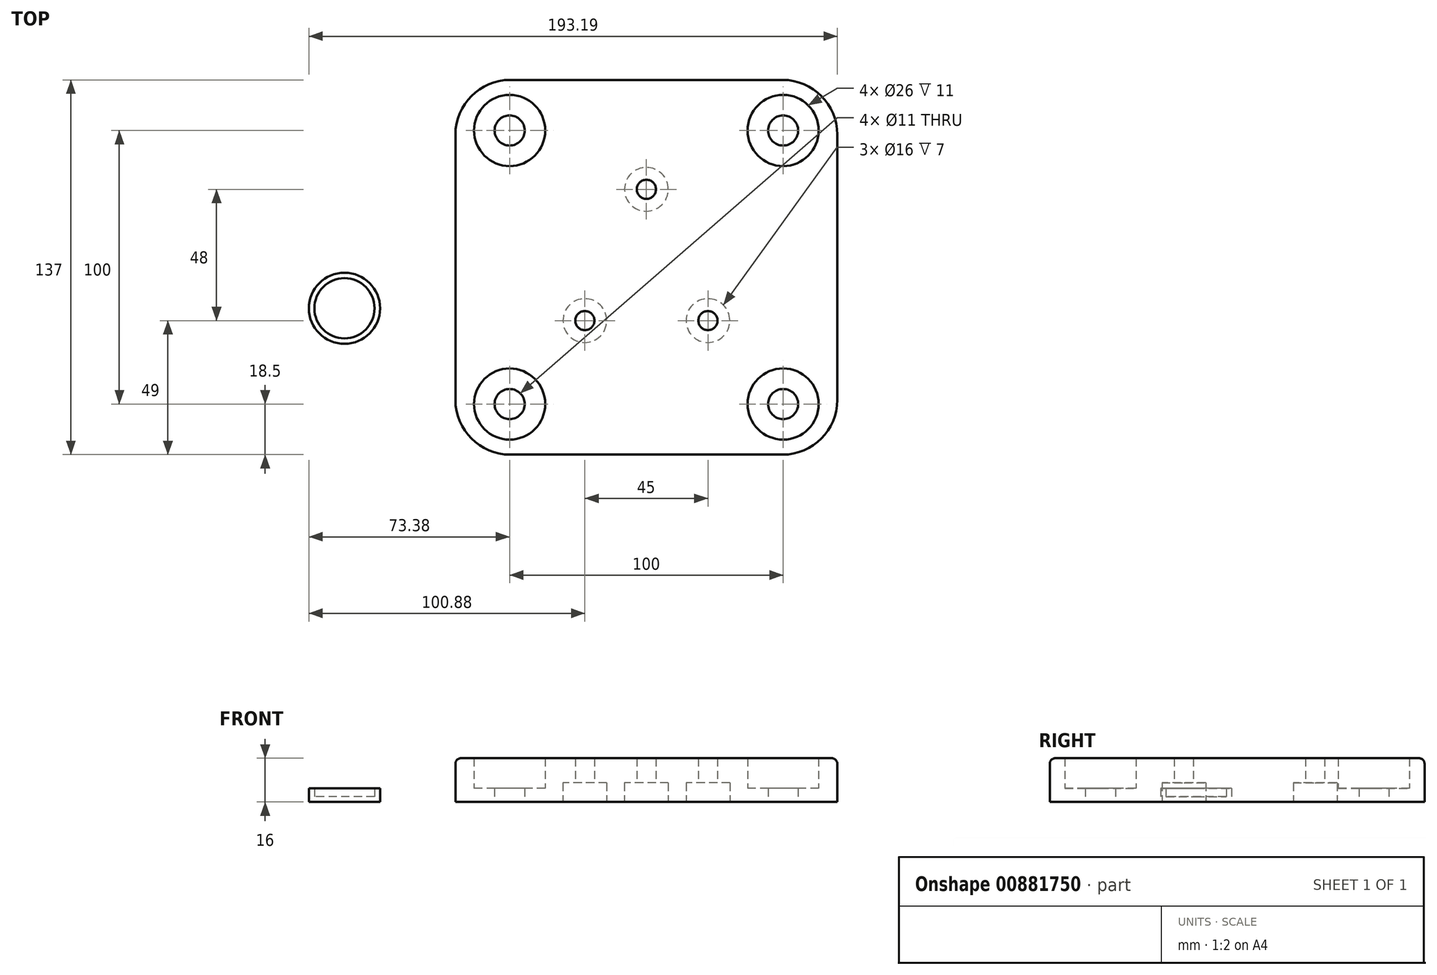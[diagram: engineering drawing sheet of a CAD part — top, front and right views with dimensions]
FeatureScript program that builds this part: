
annotation { "Feature Type Name" : "Feature", "Feature Type Description" : "" }
export const myFeature = defineFeature(function(context is Context, id is Id, definition is map)
    precondition{}
    {
        {
            var Q0;
            Q0=qCreatedBy(makeId("Top.planeOp"),FACE);
            var sketch = newSketch(context, id + "F0", { "sketchPlane" : qUnion([Q0])});
            skLineSegment(sketch, "E0", {"start": v(0, 0) * mm, "end": v(219.35, 0) * mm, "construction": true});
            skLineSegment(sketch, "E1", {"start": v(0, -100) * mm, "end": v(236.66, -100) * mm, "construction": true});
            skLineSegment(sketch, "E2", {"start": v(0, 0) * mm, "end": v(0, -167.8) * mm, "construction": true});
            skLineSegment(sketch, "E3.bottom", {"start": v(0.19, 18.5) * mm, "end": v(99.81, 18.5) * mm});
            skLineSegment(sketch, "E3.top", {"start": v(0.19, -118.5) * mm, "end": v(99.81, -118.5) * mm});
            skLineSegment(sketch, "E3.left", {"start": v(-19.81, -1.5) * mm, "end": v(-19.81, -98.5) * mm});
            skLineSegment(sketch, "E3.right", {"start": v(119.81, -1.5) * mm, "end": v(119.81, -98.5) * mm});
            skCircle(sketch, "E4", {"center": v(50, -21.5) * mm, "radius": 8 * mm});
            skCircle(sketch, "E5", {"center": v(50, -21.5) * mm, "radius": 3.5 * mm});
            skLineSegment(sketch, "E6", {"start": v(50, 18.5) * mm, "end": v(50, -118.5) * mm, "construction": true});
            skCircle(sketch, "E7", {"center": v(27.5, -69.5) * mm, "radius": 8 * mm});
            skCircle(sketch, "E8", {"center": v(27.5, -69.5) * mm, "radius": 3.5 * mm});
            skCircle(sketch, "E9", {"center": v(72.5, -69.5) * mm, "radius": 8 * mm});
            skCircle(sketch, "E10", {"center": v(72.5, -69.5) * mm, "radius": 3.5 * mm});
            skLineSegment(sketch, "E11", {"start": v(27.5, -66) * mm, "end": v(72.5, -66) * mm, "construction": true});
            skPoint(sketch, "E12.visualSharp", {"position": v(-19.81, -118.5) * mm});
            skArc(sketch, "E12.filletArc", {"start": v(-19.81, -98.5) * mm, "mid": v(-13.96, -112.64) * mm, "end": v(0.19, -118.5) * mm});
            skPoint(sketch, "E13.visualSharp", {"position": v(-19.81, 18.5) * mm});
            skArc(sketch, "E13.filletArc", {"start": v(0.19, 18.5) * mm, "mid": v(-13.96, 12.64) * mm, "end": v(-19.81, -1.5) * mm});
            skPoint(sketch, "E14.visualSharp", {"position": v(119.81, 18.5) * mm});
            skArc(sketch, "E14.filletArc", {"start": v(119.81, -1.5) * mm, "mid": v(113.96, 12.64) * mm, "end": v(99.81, 18.5) * mm});
            skPoint(sketch, "E15.visualSharp", {"position": v(119.81, -118.5) * mm});
            skArc(sketch, "E15.filletArc", {"start": v(99.81, -118.5) * mm, "mid": v(113.96, -112.64) * mm, "end": v(119.81, -98.5) * mm});
            skCircle(sketch, "E16", {"center": v(0, 0) * mm, "radius": 5.5 * mm});
            skCircle(sketch, "E17", {"center": v(100, 0) * mm, "radius": 5.5 * mm});
            skCircle(sketch, "E18", {"center": v(100, -100) * mm, "radius": 5.5 * mm});
            skCircle(sketch, "E19", {"center": v(0, -100) * mm, "radius": 5.5 * mm});
            skCircle(sketch, "E20", {"center": v(0, 0) * mm, "radius": 13 * mm});
            skCircle(sketch, "E21", {"center": v(100, 0) * mm, "radius": 13 * mm});
            skCircle(sketch, "E22", {"center": v(0, -100) * mm, "radius": 13 * mm});
            skCircle(sketch, "E23", {"center": v(100, -100) * mm, "radius": 13 * mm});
            skCircle(sketch, "E24", {"center": v(-60.38, -65) * mm, "radius": 13 * mm});
            skCircle(sketch, "E25", {"center": v(-60.38, -65) * mm, "radius": 11 * mm});
            skSolve(sketch);
        }
        {
            var Q0;
            Q0=makeQuery(id+"F0.imprint","IMPRINT",FACE,{"disambiguationData":[TD([[makeQuery(id+"F0.imprint","IMPRINT",EDGE,{"derivedFrom":sQuery(id+"F0.wireOp",EDGE,"8d677473-66c0-48cb-8076-ac21aff63ed4.0")}),-1.0]])]});
            var Q1;
            Q1=makeQuery(id+"F0.imprint","IMPRINT",FACE,{"disambiguationData":[TD([[makeQuery(id+"F0.imprint","IMPRINT",EDGE,{"derivedFrom":sQuery(id+"F0.wireOp",EDGE,"E4")}),1.0]])]});
            var Q2;
            Q2=makeQuery(id+"F0.imprint","IMPRINT",FACE,{"disambiguationData":[TD([[makeQuery(id+"F0.imprint","IMPRINT",EDGE,{"derivedFrom":sQuery(id+"F0.wireOp",EDGE,"E5")}),1.0]])]});
            var Q3;
            Q3=makeQuery(id+"F0.imprint","IMPRINT",FACE,{"disambiguationData":[TD([[makeQuery(id+"F0.imprint","IMPRINT",EDGE,{"derivedFrom":sQuery(id+"F0.wireOp",EDGE,"989b2470-fe14-45c1-91ff-a3a5b1f2c79d.0")}),-1.0]])]});
            var Q4;
            Q4=makeQuery(id+"F0.imprint","IMPRINT",FACE,{"disambiguationData":[TD([[makeQuery(id+"F0.imprint","IMPRINT",EDGE,{"derivedFrom":sQuery(id+"F0.wireOp",EDGE,"E9")}),1.0]])]});
            var Q5;
            Q5=makeQuery(id+"F0.imprint","IMPRINT",FACE,{"disambiguationData":[TD([[makeQuery(id+"F0.imprint","IMPRINT",EDGE,{"derivedFrom":sQuery(id+"F0.wireOp",EDGE,"E10")}),1.0]])]});
            var Q6;
            Q6=makeQuery(id+"F0.imprint","IMPRINT",FACE,{"disambiguationData":[TD([[makeQuery(id+"F0.imprint","IMPRINT",EDGE,{"derivedFrom":sQuery(id+"F0.wireOp",EDGE,"E7")}),1.0]])]});
            var Q7;
            Q7=makeQuery(id+"F0.imprint","IMPRINT",FACE,{"disambiguationData":[TD([[makeQuery(id+"F0.imprint","IMPRINT",EDGE,{"derivedFrom":sQuery(id+"F0.wireOp",EDGE,"E8")}),1.0]])]});
            var Q8;
            Q8=makeQuery(id+"F0.imprint","IMPRINT",FACE,{"disambiguationData":[TD([[makeQuery(id+"F0.imprint","IMPRINT",EDGE,{"derivedFrom":sQuery(id+"F0.wireOp",EDGE,"f9a4f6e7-351c-4232-8672-7d90e1cfde4a.0")}),-1.0]])]});
            var Q9;
            Q9=makeQuery(id+"F0.imprint","IMPRINT",FACE,{"disambiguationData":[TD([[makeQuery(id+"F0.imprint","IMPRINT",EDGE,{"derivedFrom":sQuery(id+"F0.wireOp",EDGE,"4f656327-ae7e-4a68-86a2-d38ab66c9fe1.0")}),-1.0]])]});
            var Q10;
            Q10=makeQuery(id+"F0.imprint","IMPRINT",FACE,{"disambiguationData":[TD([[makeQuery(id+"F0.imprint","IMPRINT",EDGE,{"derivedFrom":sQuery(id+"F0.wireOp",EDGE,"E3.bottom")}),-1.0]])]});
            extrude(context, id + "F1", {"entities" : qUnion([Q0, Q1, Q2, Q3, Q4, Q5, Q6, Q7, Q8, Q9, Q10]), "depth" : 16 * mm, "offsetDistance" : 25 * mm});
        }
        {
            var Q0;
            Q0=makeQuery(id+"F0.imprint","IMPRINT",FACE,{"disambiguationData":[TD([[makeQuery(id+"F0.imprint","IMPRINT",EDGE,{"derivedFrom":sQuery(id+"F0.wireOp",EDGE,"E9")}),1.0]])]});
            var Q1;
            Q1=makeQuery(id+"F0.imprint","IMPRINT",FACE,{"disambiguationData":[TD([[makeQuery(id+"F0.imprint","IMPRINT",EDGE,{"derivedFrom":sQuery(id+"F0.wireOp",EDGE,"E7")}),1.0]])]});
            var Q2;
            Q2=makeQuery(id+"F0.imprint","IMPRINT",FACE,{"disambiguationData":[TD([[makeQuery(id+"F0.imprint","IMPRINT",EDGE,{"derivedFrom":sQuery(id+"F0.wireOp",EDGE,"E4")}),1.0]])]});
            extrude(context, id + "F2", {"entities" : qUnion([Q0, Q1, Q2]), "operationType" : NewBodyOperationType.REMOVE, "depth" : 7 * mm, "offsetDistance" : 25 * mm});
        }
        {
            var Q0;
            Q0=makeQuery(id+"F0.imprint","IMPRINT",FACE,{"disambiguationData":[TD([[makeQuery(id+"F0.imprint","IMPRINT",EDGE,{"derivedFrom":sQuery(id+"F0.wireOp",EDGE,"E8")}),1.0]])]});
            var Q1;
            Q1=makeQuery(id+"F0.imprint","IMPRINT",FACE,{"disambiguationData":[TD([[makeQuery(id+"F0.imprint","IMPRINT",EDGE,{"derivedFrom":sQuery(id+"F0.wireOp",EDGE,"E10")}),1.0]])]});
            var Q2;
            Q2=makeQuery(id+"F0.imprint","IMPRINT",FACE,{"disambiguationData":[TD([[makeQuery(id+"F0.imprint","IMPRINT",EDGE,{"derivedFrom":sQuery(id+"F0.wireOp",EDGE,"E5")}),1.0]])]});
            var Q3;
            Q3=makeQuery(id+"F1.opExtrude","CAP_FACE",FACE,{"disambiguationData":[OSD([sQuery(id+"F0.wireOp",EDGE,"E3.bottom"),sQuery(id+"F0.wireOp",EDGE,"E3.top"),sQuery(id+"F0.wireOp",EDGE,"E3.left"),sQuery(id+"F0.wireOp",EDGE,"E3.right")])],"isStart":false});
            extrude(context, id + "F3", {"entities" : qUnion([Q0, Q1, Q2]), "operationType" : NewBodyOperationType.REMOVE, "endBound" : BoundingType.UP_TO_SURFACE, "depth" : 25 * mm, "endBoundEntityFace" : qUnion([Q3]), "offsetDistance" : 25 * mm});
        }
        {
            var Q0;
            Q0=makeQuery(id+"F1.opExtrude","CAP_EDGE",EDGE,{"disambiguationData":[OSD([sQuery(id+"F0.wireOp",EDGE,"E3.right")])],"isStart":false});
            fillet(context, id + "F4", {"entities" : qUnion([Q0]), "radius" : 2 * mm, "tangentPropagation" : true, "allowEdgeOverflow" : false});
        }
        {
            var Q0;
            Q0=makeQuery(id+"F0.imprint","IMPRINT",FACE,{"disambiguationData":[TD([[makeQuery(id+"F0.imprint","IMPRINT",EDGE,{"derivedFrom":sQuery(id+"F0.wireOp",EDGE,"E17")}),-1.0]])]});
            var Q1;
            Q1=makeQuery(id+"F0.imprint","IMPRINT",FACE,{"disambiguationData":[TD([[makeQuery(id+"F0.imprint","IMPRINT",EDGE,{"derivedFrom":sQuery(id+"F0.wireOp",EDGE,"E18")}),-1.0]])]});
            var Q2;
            Q2=makeQuery(id+"F0.imprint","IMPRINT",FACE,{"disambiguationData":[TD([[makeQuery(id+"F0.imprint","IMPRINT",EDGE,{"derivedFrom":sQuery(id+"F0.wireOp",EDGE,"E19")}),-1.0]])]});
            var Q3;
            Q3=makeQuery(id+"F0.imprint","IMPRINT",FACE,{"disambiguationData":[TD([[makeQuery(id+"F0.imprint","IMPRINT",EDGE,{"derivedFrom":sQuery(id+"F0.wireOp",EDGE,"E16")}),-1.0]])]});
            extrude(context, id + "F5", {"entities" : qUnion([Q0, Q1, Q2, Q3]), "operationType" : NewBodyOperationType.ADD, "depth" : 5 * mm, "offsetDistance" : 25 * mm});
        }
        {
            var Q0;
            Q0=makeQuery(id+"F0.imprint","IMPRINT",FACE,{"disambiguationData":[TD([[makeQuery(id+"F0.imprint","IMPRINT",EDGE,{"derivedFrom":sQuery(id+"F0.wireOp",EDGE,"E24")}),1.0]])]});
            var Q1;
            Q1=makeQuery(id+"F0.imprint","IMPRINT",FACE,{"disambiguationData":[TD([[makeQuery(id+"F0.imprint","IMPRINT",EDGE,{"derivedFrom":sQuery(id+"F0.wireOp",EDGE,"E25")}),1.0]])]});
            extrude(context, id + "F6", {"entities" : qUnion([Q0, Q1]), "depth" : 2 * mm, "offsetDistance" : 25 * mm});
        }
        {
            var Q0;
            Q0=makeQuery(id+"F0.imprint","IMPRINT",FACE,{"disambiguationData":[TD([[makeQuery(id+"F0.imprint","IMPRINT",EDGE,{"derivedFrom":sQuery(id+"F0.wireOp",EDGE,"E24")}),1.0]])]});
            extrude(context, id + "F7", {"entities" : qUnion([Q0]), "operationType" : NewBodyOperationType.ADD, "depth" : 5 * mm, "offsetDistance" : 25 * mm});
        }
    });
